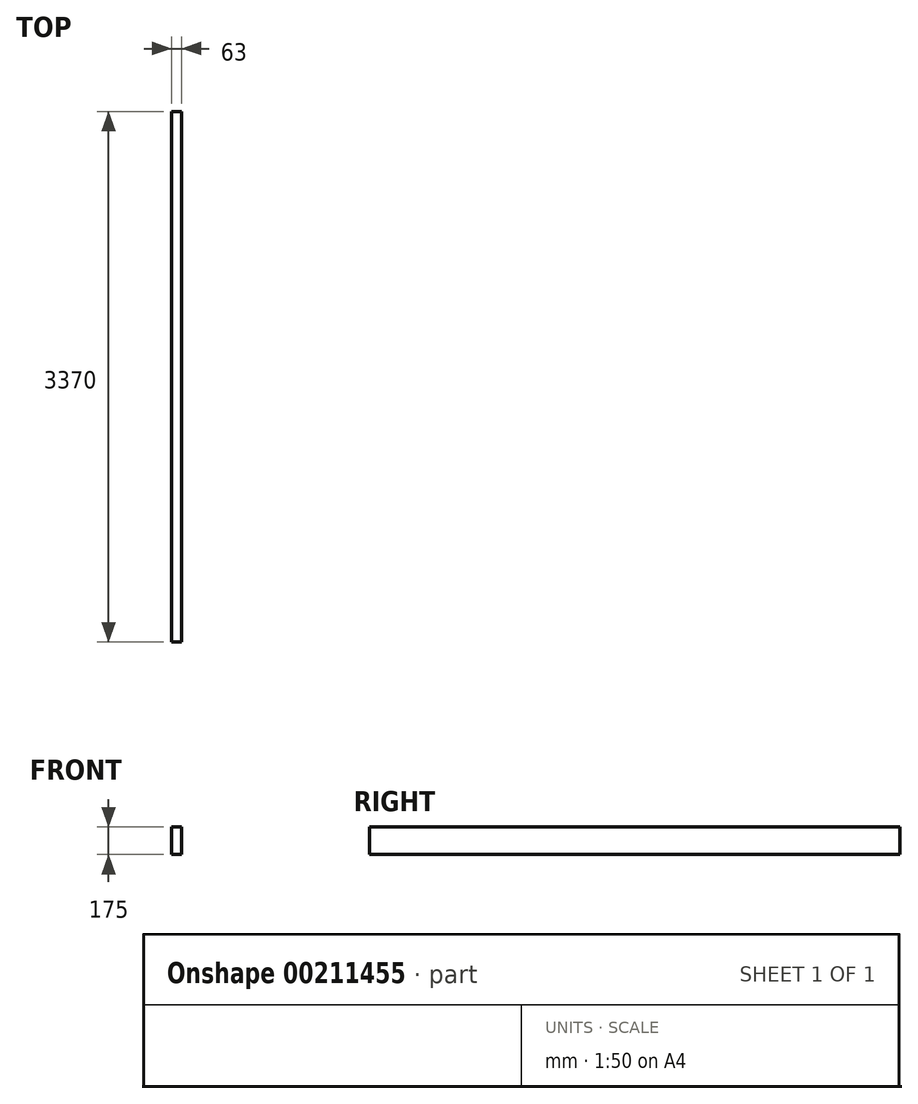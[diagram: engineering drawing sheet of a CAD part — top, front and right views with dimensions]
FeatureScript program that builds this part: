
annotation { "Feature Type Name" : "Feature", "Feature Type Description" : "" }
export const myFeature = defineFeature(function(context is Context, id is Id, definition is map)
    precondition{}
    {
        {
            var Q0;
            Q0=qCreatedBy(makeId("Front.planeOp"),FACE);
            var sketch = newSketch(context, id + "F0", { "sketchPlane" : qUnion([Q0])});
            skLineSegment(sketch, "E0.bottom", {"start": v(31.5, 87.5) * mm, "end": v(-31.5, 87.5) * mm});
            skLineSegment(sketch, "E0.top", {"start": v(31.5, -87.5) * mm, "end": v(-31.5, -87.5) * mm});
            skLineSegment(sketch, "E0.left", {"start": v(31.5, 87.5) * mm, "end": v(31.5, -87.5) * mm});
            skLineSegment(sketch, "E0.right", {"start": v(-31.5, 87.5) * mm, "end": v(-31.5, -87.5) * mm});
            skPoint(sketch, "E0.middle", {"position": v(0, 0) * mm});
            skSolve(sketch);
        }
        {
            var Q0;
            Q0=qSketchRegion(id+"F0",true);
            extrude(context, id + "F1", {"entities" : qUnion([Q0]), "depth" : (3000 + 240 + 130) * mm, "symmetric" : true});
        }
    });
